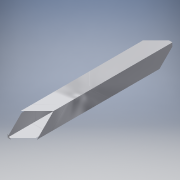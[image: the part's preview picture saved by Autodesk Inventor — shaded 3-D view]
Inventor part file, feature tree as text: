
AUTODESK INVENTOR PART (.ipt)
format: ipt  version: 2016 (Build 200138000, 138)  size: 120,320 bytes
history: native  units: in
note: dims shown in document units (in); Inventor stores cm internally (conversion verified against a paired STEP export)
features: extrude x2, sketch x2
ambient origin geometry x8: Origin, YZ Plane, XZ Plane, XY Plane, X Axis, Y Axis, Z Axis, Center Point
bodies: Solid1 (feature_tree)
feature tree (4):
  extrude  "Extrusion1"  Depth=1.0in
  extrude  "Extrusion2"  Depth=5.0in TaperAngle=0.0deg
  sketch  "Sketch1"  dims[d0=1.0in d1=1.0in]
  sketch  "Sketch2"  dims[d2=0.0625in d3=5.0in d4=0.0in d5=0.2656in d7=0.5in d8=0.5in d9=0.5in d10=1.5in d11=0.5in d12=1.5in d13=0.5in d14=0.5in d15=1.0in d16=0.0in]
